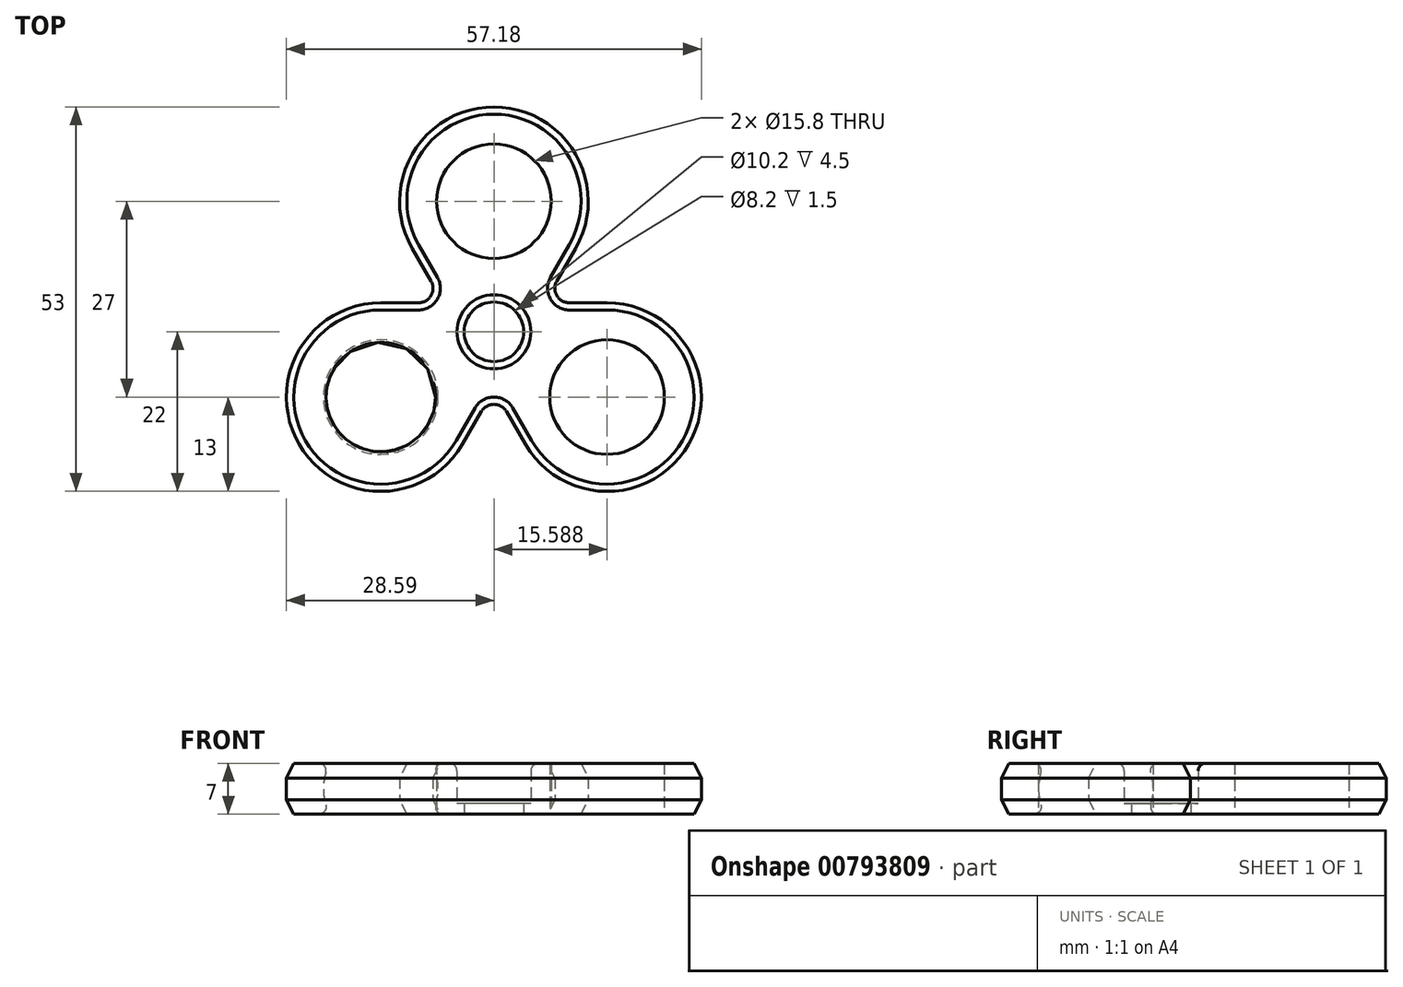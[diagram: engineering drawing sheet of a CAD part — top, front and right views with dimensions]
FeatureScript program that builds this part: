
annotation { "Feature Type Name" : "Feature", "Feature Type Description" : "" }
export const myFeature = defineFeature(function(context is Context, id is Id, definition is map)
    precondition{}
    {
        {
            var Q0;
            Q0=qCreatedBy(makeId("Top.planeOp"),FACE);
            var sketch = newSketch(context, id + "F0", { "sketchPlane" : qUnion([Q0])});
            skLineSegment(sketch, "E0", {"start": v(0, 0) * mm, "end": v(0, 18) * mm, "construction": true});
            skCircle(sketch, "E1", {"center": v(0, 18) * mm, "radius": 7.9 * mm});
            skArc(sketch, "E2", {"start": v(11.26, 11.5) * mm, "mid": v(0, 31) * mm, "end": v(-11.26, 11.5) * mm});
            skCircle(sketch, "E3", {"center": v(0, 0) * mm, "radius": 5.1 * mm});
            skArc(sketch, "E4.1.2", {"start": v(-15.59, 4) * mm, "mid": v(-26.85, -15.5) * mm, "end": v(-4.33, -15.5) * mm});
            skCircle(sketch, "E4.1.3", {"center": v(-15.59, -9) * mm, "radius": 7.9 * mm});
            skArc(sketch, "E4.2.2", {"start": v(4.33, -15.5) * mm, "mid": v(26.85, -15.5) * mm, "end": v(15.59, 4) * mm});
            skCircle(sketch, "E4.2.3", {"center": v(15.59, -9) * mm, "radius": 7.9 * mm});
            skLineSegment(sketch, "E5", {"start": v(0, 0) * mm, "end": v(-15.59, -9) * mm, "construction": true});
            skLineSegment(sketch, "E6", {"start": v(0, 0) * mm, "end": v(15.59, -9) * mm, "construction": true});
            skCircle(sketch, "E7", {"center": v(0, 0) * mm, "radius": 8 * mm, "construction": true});
            skLineSegment(sketch, "E8", {"start": v(-15.59, 4) * mm, "end": v(-6.93, 4) * mm});
            skLineSegment(sketch, "E9.MirrorCS", {"start": v(-4.33, -15.5) * mm, "end": v(0, -8) * mm});
            skLineSegment(sketch, "E10.1.0", {"start": v(4.33, -15.5) * mm, "end": v(0, -8) * mm});
            skLineSegment(sketch, "E10.1.1", {"start": v(15.59, 4) * mm, "end": v(6.93, 4) * mm});
            skLineSegment(sketch, "E10.2.0", {"start": v(11.26, 11.5) * mm, "end": v(6.93, 4) * mm});
            skLineSegment(sketch, "E10.2.1", {"start": v(-11.26, 11.5) * mm, "end": v(-6.93, 4) * mm});
            skSolve(sketch);
        }
        {
            var Q0;
            Q0=qSketchRegion(id+"F0",true);
            extrude(context, id + "F1", {"entities" : qUnion([Q0]), "depth" : 7 * mm, "offsetDistance" : 25 * mm});
        }
        {
            var Q0;
            Q0=makeQuery(id+"F1.opExtrude","SWEPT_EDGE",EDGE,{"disambiguationData":[OSD([sQuery(id+"F0.wireOp",EDGE,"hYaDFHxH-SQ1h-cJ0F-NxPf-ypNw5k6PqgM9"),sQuery(id+"F0.wireOp",EDGE,"E4.1.2")])]});
            var Q1;
            Q1=makeQuery(id+"F1.opExtrude","SWEPT_EDGE",EDGE,{"disambiguationData":[OSD([sQuery(id+"F0.wireOp",EDGE,"hYaDFHxH-SQ1h-cJ0F-NxPf-ypNw5k6PqgM9"),sQuery(id+"F0.wireOp",EDGE,"E4.2.2")])]});
            var Q2;
            Q2=makeQuery(id+"F1.opExtrude","SWEPT_EDGE",EDGE,{"disambiguationData":[OSD([sQuery(id+"F0.wireOp",EDGE,"E4.2.2"),sQuery(id+"F0.wireOp",EDGE,"79da703c-30cb-4167-bd47-66bc16433dd5.trimOffspring")])]});
            var Q3;
            Q3=makeQuery(id+"F1.opExtrude","SWEPT_EDGE",EDGE,{"disambiguationData":[OSD([sQuery(id+"F0.wireOp",EDGE,"E2"),sQuery(id+"F0.wireOp",EDGE,"79da703c-30cb-4167-bd47-66bc16433dd5.trimOffspring")])]});
            var Q4;
            Q4=makeQuery(id+"F1.opExtrude","SWEPT_EDGE",EDGE,{"disambiguationData":[OSD([sQuery(id+"F0.wireOp",EDGE,"E2"),sQuery(id+"F0.wireOp",EDGE,"007a9c35-0cf0-4482-a21c-6fcd3d696d74.trimOffspring")])]});
            var Q5;
            Q5=makeQuery(id+"F1.opExtrude","SWEPT_EDGE",EDGE,{"disambiguationData":[OSD([sQuery(id+"F0.wireOp",EDGE,"E4.1.2"),sQuery(id+"F0.wireOp",EDGE,"007a9c35-0cf0-4482-a21c-6fcd3d696d74.trimOffspring")])]});
            var Q6;
            Q6=makeQuery(id+"F1.opExtrude","SWEPT_EDGE",EDGE,{"disambiguationData":[OSD([sQuery(id+"F0.wireOp",EDGE,"E9.MirrorCS"),sQuery(id+"F0.wireOp",EDGE,"E10.1.0")])]});
            var Q7;
            Q7=makeQuery(id+"F1.opExtrude","SWEPT_EDGE",EDGE,{"disambiguationData":[OSD([sQuery(id+"F0.wireOp",EDGE,"E10.1.1"),sQuery(id+"F0.wireOp",EDGE,"E10.2.0")])]});
            var Q8;
            Q8=makeQuery(id+"F1.opExtrude","SWEPT_EDGE",EDGE,{"disambiguationData":[OSD([sQuery(id+"F0.wireOp",EDGE,"E8"),sQuery(id+"F0.wireOp",EDGE,"E10.2.1")])]});
            fillet(context, id + "F2", {"entities" : qUnion([Q0, Q1, Q2, Q3, Q4, Q5, Q6, Q7, Q8]), "radius" : 2 * mm, "tangentPropagation" : true, "allowEdgeOverflow" : false});
        }
        {
            var Q0;
            Q0=makeQuery(id+"F1.opExtrude","CAP_EDGE",EDGE,{"disambiguationData":[OSD([sQuery(id+"F0.wireOp",EDGE,"E4.2.2")])],"isStart":true});
            var Q1;
            Q1=makeQuery(id+"F1.opExtrude","CAP_EDGE",EDGE,{"disambiguationData":[OSD([sQuery(id+"F0.wireOp",EDGE,"E4.2.2")])],"isStart":false});
            chamfer(context, id + "F3", {"entities" : qUnion([Q0, Q1]), "chamferType" : ChamferType.TWO_OFFSETS, "width1" : 2 * mm, "oppositeDirection" : false, "width2" : 1 * mm, "tangentPropagation" : true});
        }
        {
            var Q0;
            Q0=qCreatedBy(makeId("Top.planeOp"),FACE);
            var sketch = newSketch(context, id + "F4", { "sketchPlane" : qUnion([Q0])});
            skCircle(sketch, "E11.0", {"center": v(-15.59, -9) * mm, "radius": 7.9 * mm, "construction": true});
            skLineSegment(sketch, "E12", {"start": v(0, 0) * mm, "end": v(-15.59, -9) * mm, "construction": true});
            skCircle(sketch, "E13.0", {"center": v(0, 18) * mm, "radius": 7.9 * mm, "construction": true});
            skLineSegment(sketch, "E14", {"start": v(0, 0) * mm, "end": v(0, 18) * mm, "construction": true});
            skCircle(sketch, "E15.0", {"center": v(15.59, -9) * mm, "radius": 7.9 * mm, "construction": true});
            skLineSegment(sketch, "E16", {"start": v(0, 0) * mm, "end": v(15.59, -9) * mm, "construction": true});
            skSolve(sketch);
        }
        {
            var Q0;
            {var subQ0=sQuery(id+"F0.wireOp",EDGE,"E4.1.2");Q0=makeQuery(id+"F3.opChamfer","BLEND_EDGE",EDGE,{"blendedFrom":[makeQuery(id+"F1.opExtrude","CAP_EDGE",EDGE,{"disambiguationData":[OSD([subQ0])],"isStart":false}),makeQuery(id+"F1.opExtrude","CAP_FACE",FACE,{"disambiguationData":[OSD([sQuery(id+"F0.wireOp",EDGE,"E1"),sQuery(id+"F0.wireOp",EDGE,"E2"),sQuery(id+"F0.wireOp",EDGE,"E3"),sQuery(id+"F0.wireOp",EDGE,"hYaDFHxH-SQ1h-cJ0F-NxPf-ypNw5k6PqgM9"),subQ0,sQuery(id+"F0.wireOp",EDGE,"E4.1.3"),sQuery(id+"F0.wireOp",EDGE,"E4.2.2"),sQuery(id+"F0.wireOp",EDGE,"E4.2.3"),sQuery(id+"F0.wireOp",EDGE,"79da703c-30cb-4167-bd47-66bc16433dd5.trimOffspring"),sQuery(id+"F0.wireOp",EDGE,"007a9c35-0cf0-4482-a21c-6fcd3d696d74.trimOffspring")])],"isStart":false})],"blendedInto":[makeQuery(id+"F1.opExtrude","CAP_FACE",FACE,{"disambiguationData":[OSD([sQuery(id+"F0.wireOp",EDGE,"E1"),sQuery(id+"F0.wireOp",EDGE,"E2"),sQuery(id+"F0.wireOp",EDGE,"E3"),sQuery(id+"F0.wireOp",EDGE,"hYaDFHxH-SQ1h-cJ0F-NxPf-ypNw5k6PqgM9"),subQ0,sQuery(id+"F0.wireOp",EDGE,"E4.1.3"),sQuery(id+"F0.wireOp",EDGE,"E4.2.2"),sQuery(id+"F0.wireOp",EDGE,"E4.2.3"),sQuery(id+"F0.wireOp",EDGE,"79da703c-30cb-4167-bd47-66bc16433dd5.trimOffspring"),sQuery(id+"F0.wireOp",EDGE,"007a9c35-0cf0-4482-a21c-6fcd3d696d74.trimOffspring")])],"isStart":false})]});}
            cPoint(context, id + "F5", {"entities" : qUnion([Q0]), "parameter" : 0.5});
        }
        {
            var Q0;
            Q0=sQuery(id+"F4.wireOp",VERTEX,"E12.start");
            var Q1;
            Q1=sQuery(id+"F4.wireOp",VERTEX,"E11.0.center");
            var Q2;
            Q2=qCreatedBy(id+"F5",VERTEX);
            cPlane(context, id + "F6", {"entities" : qUnion([Q0, Q1, Q2]), "cplaneType" : CPlaneType.THREE_POINT, "offset" : 25 * mm, "width" : 150 * mm, "height" : 150 * mm});
        }
        {
            var Q0;
            Q0=qCreatedBy(id+"F6.planeOp",FACE);
            var sketch = newSketch(context, id + "F7", { "sketchPlane" : qUnion([Q0])});
            skLineSegment(sketch, "E17.0", {"start": v(-25.9, 7) * mm, "end": v(-25.08, 7) * mm, "construction": true});
            skLineSegment(sketch, "E18.1", {"start": v(-25.9, 0) * mm, "end": v(-25.08, 0) * mm, "construction": true});
            skLineSegment(sketch, "E19", {"start": v(-25.9, 7) * mm, "end": v(-25.9, 0) * mm});
            skLineSegment(sketch, "E20", {"start": v(-18, 0) * mm, "end": v(-18, 7) * mm, "construction": true});
            skArc(sketch, "E21", {"start": v(-25.08, 7) * mm, "mid": v(-25.9, 3.5) * mm, "end": v(-25.08, 0) * mm});
            skLineSegment(sketch, "E22", {"start": v(-25.9, 7) * mm, "end": v(-25.08, 7) * mm});
            skLineSegment(sketch, "E23", {"start": v(-25.9, 0) * mm, "end": v(-25.08, 0) * mm});
            skLineSegment(sketch, "E24.trimOffspring", {"start": v(-18, 7) * mm, "end": v(-10.1, 7) * mm, "construction": true});
            skLineSegment(sketch, "E25.trimOffspring", {"start": v(-18, 0) * mm, "end": v(-10.1, 0) * mm, "construction": true});
            skSolve(sketch);
        }
        {
            var Q0;
            Q0=qSketchRegion(id+"F7",true);
            var Q1;
            Q1=sQuery(id+"F7.wireOp",EDGE,"E20");
            revolve(context, id + "F8", {"operationType" : NewBodyOperationType.ADD, "surfaceOperationType" : NewSurfaceOperationType.NEW, "entities" : qUnion([Q0]), "axis" : qUnion([Q1]), "revolveType" : RevolveType.FULL});
        }
        {
            var Q0;
            Q0=makeQuery(id+"F8.opRevolve","SWEPT_EDGE",EDGE,{"disambiguationData":[OSD([sQuery(id+"F7.wireOp",EDGE,"E21"),sQuery(id+"F7.wireOp",EDGE,"E22")])]});
            var Q1;
            Q1=makeQuery(id+"F8.opRevolve","SWEPT_EDGE",EDGE,{"disambiguationData":[OSD([sQuery(id+"F7.wireOp",EDGE,"E21"),sQuery(id+"F7.wireOp",EDGE,"E23")])]});
            var Q2;
            Q2=makeQuery(id+"Fynh9oEJvHPlE7w_1.2.F8.opRevolve","SWEPT_EDGE",EDGE,{"disambiguationData":[OSD([sQuery(id+"F7.wireOp",EDGE,"E21"),sQuery(id+"F7.wireOp",EDGE,"E22")])]});
            var Q3;
            Q3=makeQuery(id+"Fynh9oEJvHPlE7w_1.2.F8.opRevolve","SWEPT_EDGE",EDGE,{"disambiguationData":[OSD([sQuery(id+"F7.wireOp",EDGE,"E21"),sQuery(id+"F7.wireOp",EDGE,"E23")])]});
            var Q4;
            Q4=makeQuery(id+"Fynh9oEJvHPlE7w_1.1.F8.opRevolve","SWEPT_EDGE",EDGE,{"disambiguationData":[OSD([sQuery(id+"F7.wireOp",EDGE,"E21"),sQuery(id+"F7.wireOp",EDGE,"E22")])]});
            var Q5;
            Q5=makeQuery(id+"Fynh9oEJvHPlE7w_1.1.F8.opRevolve","SWEPT_EDGE",EDGE,{"disambiguationData":[OSD([sQuery(id+"F7.wireOp",EDGE,"E21"),sQuery(id+"F7.wireOp",EDGE,"E23")])]});
            var Q6;
            Q6=makeQuery(id+"F1.opExtrude","CAP_EDGE",EDGE,{"disambiguationData":[OSD([sQuery(id+"F0.wireOp",EDGE,"E3")])],"isStart":false});
            fillet(context, id + "F9", {"entities" : qUnion([Q0, Q1, Q2, Q3, Q4, Q5, Q6]), "radius" : 1 * mm, "tangentPropagation" : true, "allowEdgeOverflow" : false});
        }
        {
            var Q0;
            Q0=qCreatedBy(makeId("Top.planeOp"),FACE);
            var sketch = newSketch(context, id + "F10", { "sketchPlane" : qUnion([Q0])});
            skCircle(sketch, "E26.0", {"center": v(0, 0) * mm, "radius": 5.1 * mm});
            skCircle(sketch, "E27", {"center": v(0, 0) * mm, "radius": 4.1 * mm});
            skSolve(sketch);
        }
        {
            var Q0;
            Q0=qSketchRegion(id+"F10",true);
            extrude(context, id + "F11", {"entities" : qUnion([Q0]), "operationType" : NewBodyOperationType.ADD, "depth" : 1.5 * mm, "offsetDistance" : 25 * mm});
        }
    });
